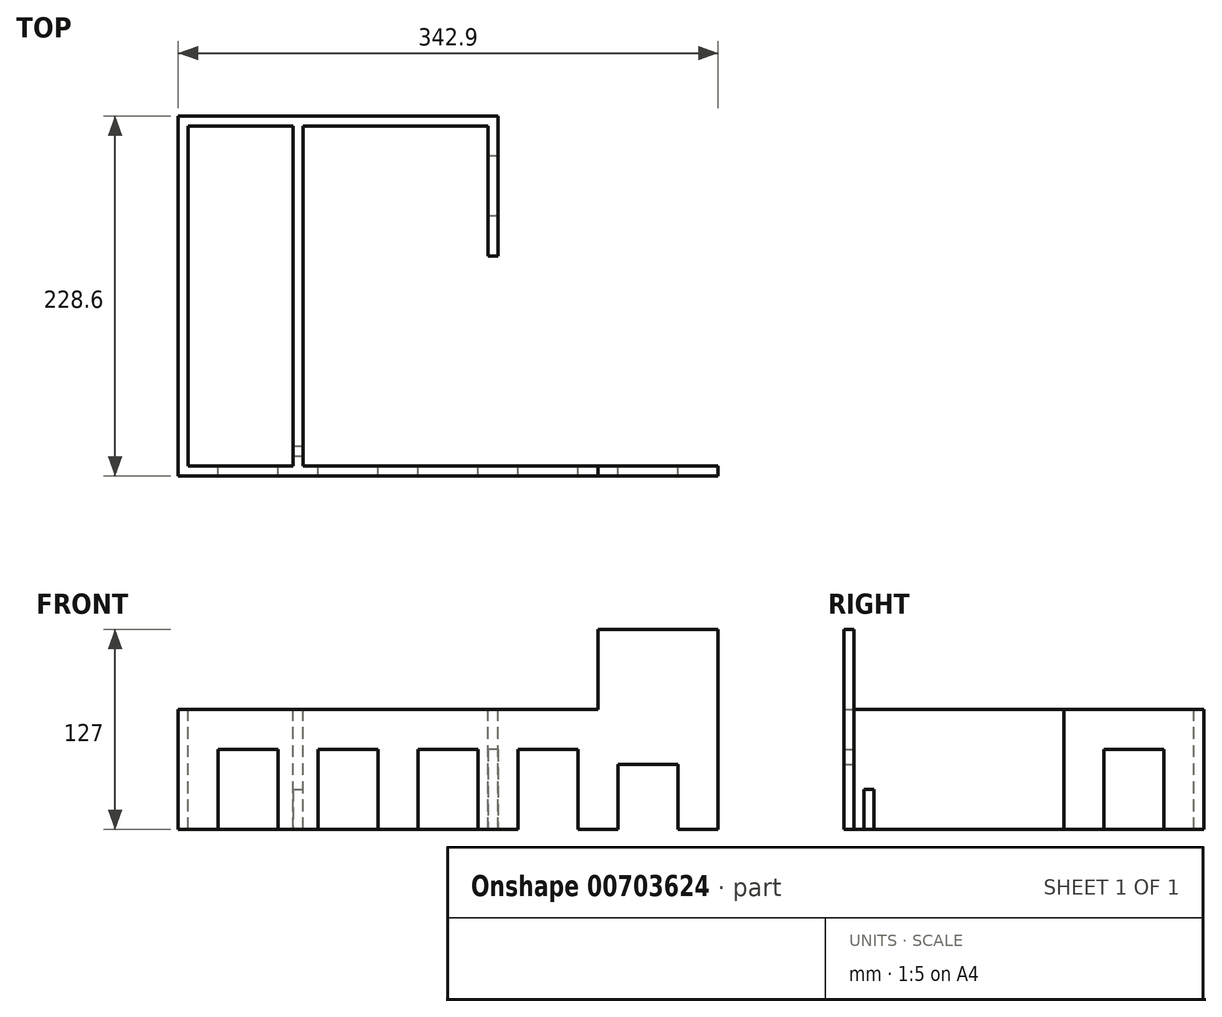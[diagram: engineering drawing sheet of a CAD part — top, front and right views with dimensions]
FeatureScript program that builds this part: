
annotation { "Feature Type Name" : "Feature", "Feature Type Description" : "" }
export const myFeature = defineFeature(function(context is Context, id is Id, definition is map)
    precondition{}
    {
        {
            var Q0;
            Q0=qCreatedBy(makeId("Front.planeOp"),FACE);
            var sketch = newSketch(context, id + "F0", { "sketchPlane" : qUnion([Q0])});
            skLineSegment(sketch, "E0", {"start": v(0, 0) * mm, "end": v(25.4, 0) * mm});
            skLineSegment(sketch, "E1", {"start": v(63.5, 0) * mm, "end": v(88.9, 0) * mm});
            skLineSegment(sketch, "E2", {"start": v(127, 0) * mm, "end": v(152.4, 0) * mm});
            skLineSegment(sketch, "E3", {"start": v(152.4, 0) * mm, "end": v(152.4, 50.8) * mm});
            skLineSegment(sketch, "E4", {"start": v(152.4, 50.8) * mm, "end": v(190.5, 50.8) * mm});
            skLineSegment(sketch, "E5", {"start": v(190.5, 50.8) * mm, "end": v(190.5, 0) * mm});
            skLineSegment(sketch, "E6", {"start": v(190.5, 0) * mm, "end": v(215.9, 0) * mm});
            skLineSegment(sketch, "E7", {"start": v(215.9, 0) * mm, "end": v(215.9, 50.8) * mm});
            skLineSegment(sketch, "E8", {"start": v(215.9, 50.8) * mm, "end": v(254, 50.8) * mm});
            skLineSegment(sketch, "E9", {"start": v(254, 50.8) * mm, "end": v(254, 0) * mm});
            skLineSegment(sketch, "E10", {"start": v(254, 0) * mm, "end": v(279.4, 0) * mm});
            skLineSegment(sketch, "E11", {"start": v(279.4, 0) * mm, "end": v(279.4, 41.27) * mm});
            skLineSegment(sketch, "E12", {"start": v(279.4, 41.27) * mm, "end": v(317.5, 41.28) * mm});
            skLineSegment(sketch, "E13", {"start": v(317.5, 41.28) * mm, "end": v(317.5, 0) * mm});
            skLineSegment(sketch, "E14", {"start": v(317.5, 0) * mm, "end": v(342.9, 0) * mm});
            skLineSegment(sketch, "E15", {"start": v(342.9, 0) * mm, "end": v(342.9, 127) * mm});
            skLineSegment(sketch, "E16", {"start": v(88.9, 0) * mm, "end": v(88.9, 50.8) * mm});
            skLineSegment(sketch, "E17", {"start": v(88.9, 50.8) * mm, "end": v(127, 50.8) * mm});
            skLineSegment(sketch, "E18", {"start": v(127, 50.8) * mm, "end": v(127, 0) * mm});
            skLineSegment(sketch, "E19", {"start": v(25.4, 0) * mm, "end": v(25.4, 50.8) * mm});
            skLineSegment(sketch, "E20", {"start": v(25.4, 50.8) * mm, "end": v(63.5, 50.8) * mm});
            skLineSegment(sketch, "E21", {"start": v(63.5, 50.8) * mm, "end": v(63.5, 0) * mm});
            skLineSegment(sketch, "E22", {"start": v(0, 0) * mm, "end": v(0, 76.2) * mm});
            skLineSegment(sketch, "E23", {"start": v(342.9, 127) * mm, "end": v(266.7, 127) * mm});
            skLineSegment(sketch, "E24", {"start": v(266.7, 76.2) * mm, "end": v(266.7, 127) * mm});
            skLineSegment(sketch, "E25", {"start": v(0, 76.2) * mm, "end": v(266.7, 76.2) * mm});
            skSolve(sketch);
        }
        {
            var Q0;
            Q0 = qSketchRegion(id + "F0", true);
            extrude(context, id + "F1", {"entities" : qUnion([Q0]), "depth" : 6.35 * mm, "offsetDistance" : 25.4 * mm});
        }
        {
            var Q0;
            Q0=qCreatedBy(makeId("Right.planeOp"),FACE);
            var sketch = newSketch(context, id + "F2", { "sketchPlane" : qUnion([Q0])});
            skLineSegment(sketch, "E26.bottom", {"start": v(0, 0) * mm, "end": v(215.9, 0) * mm});
            skLineSegment(sketch, "E26.top", {"start": v(0, 76.2) * mm, "end": v(215.9, 76.2) * mm});
            skLineSegment(sketch, "E26.left", {"start": v(0, 0) * mm, "end": v(0, 76.2) * mm});
            skLineSegment(sketch, "E26.right", {"start": v(215.9, 0) * mm, "end": v(215.9, 76.2) * mm});
            skSolve(sketch);
        }
        {
            var Q0;
            Q0 = qSketchRegion(id + "F2", true);
            extrude(context, id + "F3", {"entities" : qUnion([Q0]), "operationType" : NewBodyOperationType.ADD, "depth" : 6.35 * mm, "offsetDistance" : 25.4 * mm});
        }
        {
            var Q0;
            Q0=makeQuery(id+"F3.opExtrude","SWEPT_FACE",FACE,{"disambiguationData":[OSD([sQuery(id+"F2.wireOp",EDGE,"E26.right")])]});
            var sketch = newSketch(context, id + "F4", { "sketchPlane" : qUnion([Q0])});
            skLineSegment(sketch, "E27.bottom", {"start": v(0, 0) * mm, "end": v(-196.85, 0) * mm});
            skLineSegment(sketch, "E27.top", {"start": v(0, 76.2) * mm, "end": v(-196.85, 76.2) * mm});
            skLineSegment(sketch, "E27.left", {"start": v(0, 0) * mm, "end": v(0, 76.2) * mm});
            skLineSegment(sketch, "E27.right", {"start": v(-196.85, 0) * mm, "end": v(-196.85, 76.2) * mm});
            skSolve(sketch);
        }
        {
            var Q0;
            Q0 = qSketchRegion(id + "F4", true);
            extrude(context, id + "F5", {"entities" : qUnion([Q0]), "operationType" : NewBodyOperationType.ADD, "depth" : 6.35 * mm, "offsetDistance" : 25.4 * mm});
        }
        {
            var Q0;
            Q0=makeQuery(id+"F5.opExtrude","SWEPT_FACE",FACE,{"disambiguationData":[OSD([sQuery(id+"F4.wireOp",EDGE,"E27.right")])]});
            var sketch = newSketch(context, id + "F6", { "sketchPlane" : qUnion([Q0])});
            skLineSegment(sketch, "E28", {"start": v(222.25, 76.2) * mm, "end": v(222.25, 0) * mm});
            skLineSegment(sketch, "E29", {"start": v(222.25, 0) * mm, "end": v(196.85, 0) * mm});
            skPoint(sketch, "E29.endSnap0", {"position": v(219.07, 0) * mm});
            skLineSegment(sketch, "E30", {"start": v(196.85, 0) * mm, "end": v(196.85, 50.8) * mm});
            skLineSegment(sketch, "E31", {"start": v(196.85, 50.8) * mm, "end": v(158.75, 50.8) * mm});
            skLineSegment(sketch, "E32", {"start": v(158.75, 50.8) * mm, "end": v(158.75, 0) * mm});
            skLineSegment(sketch, "E33", {"start": v(158.75, 0) * mm, "end": v(133.35, 0) * mm});
            skLineSegment(sketch, "E34", {"start": v(133.35, 0) * mm, "end": v(133.35, 76.2) * mm});
            skLineSegment(sketch, "E35", {"start": v(133.35, 76.2) * mm, "end": v(222.25, 76.2) * mm});
            skSolve(sketch);
        }
        {
            var Q0;
            Q0 = qSketchRegion(id + "F6", true);
            extrude(context, id + "F7", {"entities" : qUnion([Q0]), "operationType" : NewBodyOperationType.ADD, "depth" : 6.35 * mm, "offsetDistance" : 25.4 * mm});
        }
        {
            var Q0;
            Q0=makeQuery(id+"F7.boolean.opBoolean","MERGE",FACE,{"derivedFrom":[makeQuery(id+"F5.boolean.opBoolean","MERGE",FACE,{"derivedFrom":[makeQuery(id+"F3.boolean.opBoolean","MERGE",FACE,{"derivedFrom":[makeQuery(id+"F1.opExtrude","SWEPT_FACE",FACE,{"disambiguationData":[OSD([sQuery(id+"F0.wireOp",EDGE,"E25")])]}),makeQuery(id+"F3.opExtrude","SWEPT_FACE",FACE,{"disambiguationData":[OSD([sQuery(id+"F2.wireOp",EDGE,"E26.top")])]})]}),makeQuery(id+"F5.opExtrude","SWEPT_FACE",FACE,{"disambiguationData":[OSD([sQuery(id+"F4.wireOp",EDGE,"E27.top")])]})]}),makeQuery(id+"F7.opExtrude","SWEPT_FACE",FACE,{"disambiguationData":[OSD([sQuery(id+"F6.wireOp",EDGE,"E35")])]})]});
            var sketch = newSketch(context, id + "F8", { "sketchPlane" : qUnion([Q0])});
            skLineSegment(sketch, "E36.bottom", {"start": v(73.03, 215.9) * mm, "end": v(79.37, 215.9) * mm});
            skLineSegment(sketch, "E36.top", {"start": v(73.02, 0) * mm, "end": v(79.37, 0) * mm});
            skLineSegment(sketch, "E36.left", {"start": v(73.02, 215.9) * mm, "end": v(73.02, 0) * mm});
            skLineSegment(sketch, "E36.right", {"start": v(79.37, 215.9) * mm, "end": v(79.37, 0) * mm});
            skSolve(sketch);
        }
        {
            var Q0;
            Q0=makeQuery(id+"F8.imprint","IMPRINT",FACE,{"disambiguationData":[TD([[makeQuery(id+"F8.imprint","IMPRINT",EDGE,{"derivedFrom":sQuery(id+"F8.wireOp",EDGE,"E36.bottom")}),-1.0]])]});
            extrude(context, id + "F9", {"entities" : qUnion([Q0]), "operationType" : NewBodyOperationType.ADD, "oppositeDirection" : true, "depth" : 76.2 * mm, "offsetDistance" : 25.4 * mm});
        }
        {
            var Q0;
            Q0=makeQuery(id+"F9.opExtrude","SWEPT_FACE",FACE,{"disambiguationData":[OSD([sQuery(id+"F8.wireOp",EDGE,"E36.right")])]});
            var sketch = newSketch(context, id + "F10", { "sketchPlane" : qUnion([Q0])});
            skLineSegment(sketch, "E37.bottom", {"start": v(6.35, 0) * mm, "end": v(12.7, 0) * mm});
            skLineSegment(sketch, "E37.top", {"start": v(6.35, 25.4) * mm, "end": v(12.7, 25.4) * mm});
            skLineSegment(sketch, "E37.left", {"start": v(6.35, 0) * mm, "end": v(6.35, 25.4) * mm});
            skLineSegment(sketch, "E37.right", {"start": v(12.7, 0) * mm, "end": v(12.7, 25.4) * mm});
            skSolve(sketch);
        }
        {
            var Q0;
            Q0 = qSketchRegion(id + "F10", true);
            extrude(context, id + "F11", {"entities" : qUnion([Q0]), "operationType" : NewBodyOperationType.REMOVE, "oppositeDirection" : true, "depth" : 12.7 * mm, "offsetDistance" : 25.4 * mm});
        }
    });
